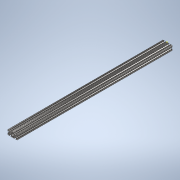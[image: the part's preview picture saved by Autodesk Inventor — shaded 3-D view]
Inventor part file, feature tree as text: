
AUTODESK INVENTOR PART (.ipt)
format: ipt  version: 2020 (Build 240168000, 168)  size: 358,912 bytes
history: native  units: in
note: dims shown in document units (in); Inventor stores cm internally (conversion verified against a paired STEP export)
features: sketch x2, extrude x1
ambient origin geometry x8: Origin, YZ Plane, XZ Plane, XY Plane, X Axis, Y Axis, Z Axis, Center Point
bodies: Solid1 (feature_tree)
feature tree (3):
  extrude  "Extrusion1"  [1 undecoded]
  sketch  "Sketch2"
  sketch  "Sketch1"  dims[d0=32.0in d1=0.0in]
note: 1 required parameter value undecoded (feature->parameter linkage not recoverable at this tier; creation-order binding heuristic only, values carry confidence <= 0.55)
